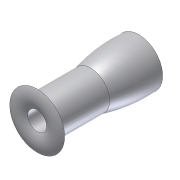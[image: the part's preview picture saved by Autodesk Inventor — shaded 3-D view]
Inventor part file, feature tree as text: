
AUTODESK INVENTOR PART (.ipt)
format: ipt  version: 2012 (Build 160160000, 160)  size: 120,832 bytes
history: native  units: in
note: dims shown in document units (in); Inventor stores cm internally (conversion verified against a paired STEP export)
features: sketch x3, revolve x2, projected_geometry x2, extrude x1, plane x1, other x1
ambient origin geometry x8: Origin, YZ Plane, XZ Plane, XY Plane, X Axis, Y Axis, Z Axis, Center Point
bodies: Solid1 (feature_tree)
feature tree (10):
  extrude  "Extrusion1"  Depth=0.5in TaperAngle=0.0deg
  plane  "Work Plane1"
  revolve  "Revolution1"  Angle=90.0deg
  revolve  "Revolution3"  [1 undecoded]
  sketch  "Sketch1"  dims[d0=0.1875in d1=0.5in d2=0.0in]
  other  "Work Axis1"
  sketch  "Sketch2"  dims[d3=90.0deg d4=90.0deg]
  projected_geometry  "Projected Loop1"
  sketch  "Sketch3"  dims[d6=90.0deg]
  projected_geometry  "Project Cut Edges1"
note: 1 required parameter value undecoded (feature->parameter linkage not recoverable at this tier; creation-order binding heuristic only, values carry confidence <= 0.55)
